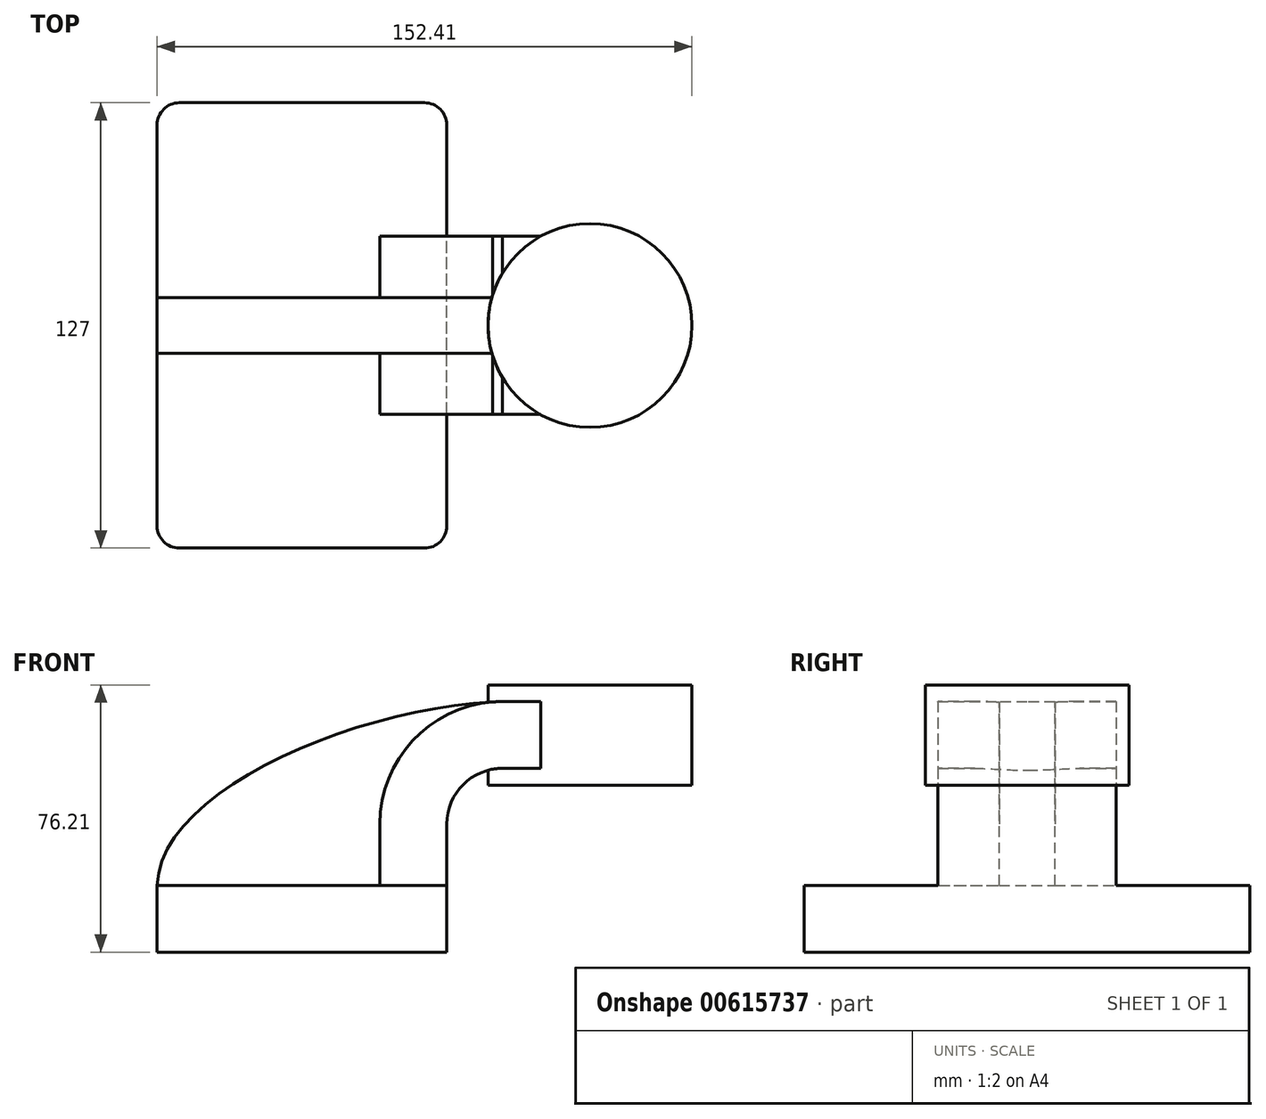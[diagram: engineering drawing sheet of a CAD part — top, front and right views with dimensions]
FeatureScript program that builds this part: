
annotation { "Feature Type Name" : "Feature", "Feature Type Description" : "" }
export const myFeature = defineFeature(function(context is Context, id is Id, definition is map)
    precondition{}
    {
        {
            var Q0;
            Q0=qCreatedBy(makeId("Front.planeOp"),FACE);
            var sketch = newSketch(context, id + "F0", { "sketchPlane" : qUnion([Q0])});
            skLineSegment(sketch, "E0.bottom", {"start": v(-41.27, -9.53) * mm, "end": v(41.28, -9.53) * mm});
            skLineSegment(sketch, "E0.top", {"start": v(-41.28, 9.52) * mm, "end": v(41.28, 9.52) * mm});
            skLineSegment(sketch, "E0.left", {"start": v(-41.28, -9.53) * mm, "end": v(-41.28, 9.53) * mm});
            skLineSegment(sketch, "E0.right", {"start": v(41.28, -9.53) * mm, "end": v(41.28, 9.52) * mm});
            skPoint(sketch, "E0.middle", {"position": v(0, 0) * mm});
            skLineSegment(sketch, "E1.bottom", {"start": v(60.32, 38.1) * mm, "end": v(111.12, 38.1) * mm});
            skLineSegment(sketch, "E1.top", {"start": v(60.32, 66.67) * mm, "end": v(111.12, 66.67) * mm});
            skLineSegment(sketch, "E1.left", {"start": v(60.32, 38.1) * mm, "end": v(60.32, 66.67) * mm});
            skLineSegment(sketch, "E1.right", {"start": v(111.12, 38.1) * mm, "end": v(111.12, 66.67) * mm});
            skPoint(sketch, "E1.middle", {"position": v(85.72, 52.39) * mm});
            skLineSegment(sketch, "E2", {"start": v(41.28, 9.52) * mm, "end": v(41.28, 27) * mm});
            skArc(sketch, "E3", {"start": v(57.15, 42.88) * mm, "mid": v(45.92, 38.23) * mm, "end": v(41.27, 27) * mm});
            skLineSegment(sketch, "E4", {"start": v(57.15, 42.88) * mm, "end": v(82.07, 42.88) * mm});
            skLineSegment(sketch, "E5.0", {"start": v(57.15, 61.93) * mm, "end": v(82.07, 61.93) * mm});
            skArc(sketch, "E5.1", {"start": v(57.15, 61.93) * mm, "mid": v(32.45, 51.7) * mm, "end": v(22.22, 27) * mm});
            skLineSegment(sketch, "E5.2", {"start": v(22.22, 9.52) * mm, "end": v(22.22, 27) * mm});
            skFitSpline(sketch, "E6", {"points": [v(-41.27, 9.53) * mm, v(57.15, 61.93) * mm], "startDerivative": vector(2.8, 83.11) * mm, "endDerivative": vector(120.3, 3.3) * mm});
            skLineSegment(sketch, "E7", {"start": v(82.07, 38.1) * mm, "end": v(82.07, 66.67) * mm});
            skSolve(sketch);
        }
        {
            var Q0;
            Q0=makeQuery(id+"F0.imprint","IMPRINT",FACE,{"disambiguationData":[TD([[makeQuery(id+"F0.imprint","IMPRINT",EDGE,{"derivedFrom":sQuery(id+"F0.wireOp",EDGE,"E0.bottom")}),1.0]])]});
            extrude(context, id + "F1", {"entities" : qUnion([Q0]), "endBound" : BoundingType.SYMMETRIC, "depth" : 127 * mm, "offsetDistance" : 25.4 * mm});
        }
        {
            var Q0;
            {var subQ1=sQuery(id+"F0.wireOp",EDGE,"E2");Q0=makeQuery(id+"F0.imprint","IMPRINT",FACE,{"disambiguationData":[TD([[makeQuery(id+"F0.imprint","IMPRINT",EDGE,{"derivedFrom":subQ1}),1.0]])]});}
            var Q1;
            {var subQ0=sQuery(id+"F0.wireOp",EDGE,"E4");var subQ1=sQuery(id+"F0.wireOp",EDGE,"E1.left");var subQ2=makeQuery(id+"F0.imprint","INTERSECT",VERTEX,{"derivedFrom":[subQ1,subQ0]});Q1=makeQuery(id+"F0.imprint","IMPRINT",FACE,{"disambiguationData":[TD([[makeQuery(id+"F0.imprint","IMPRINT",EDGE,{"disambiguationData":[TD([[subQ2,-1.0]])],"derivedFrom":subQ1}),-1.0]])]});}
            extrude(context, id + "F2", {"entities" : qUnion([Q0, Q1]), "operationType" : NewBodyOperationType.ADD, "endBound" : BoundingType.SYMMETRIC, "depth" : 50.8 * mm, "offsetDistance" : 25.4 * mm});
        }
        {
            var Q0;
            {var subQ3=sQuery(id+"F0.wireOp",EDGE,"E5.2");Q0=makeQuery(id+"F0.imprint","IMPRINT",FACE,{"disambiguationData":[TD([[makeQuery(id+"F0.imprint","IMPRINT",EDGE,{"derivedFrom":subQ3}),1.0]])]});}
            extrude(context, id + "F3", {"entities" : qUnion([Q0]), "operationType" : NewBodyOperationType.ADD, "endBound" : BoundingType.SYMMETRIC, "depth" : 15.88 * mm, "offsetDistance" : 25.4 * mm});
        }
        {
            var Q0;
            {var subQ4=sQuery(id+"F0.wireOp",EDGE,"E1.right");Q0=makeQuery(id+"F0.imprint","IMPRINT",FACE,{"disambiguationData":[TD([[makeQuery(id+"F0.imprint","IMPRINT",EDGE,{"derivedFrom":subQ4}),1.0]])]});}
            var Q1;
            Q1=sQuery(id+"F0.wireOp",EDGE,"E7");
            revolve(context, id + "F4", {"operationType" : NewBodyOperationType.ADD, "entities" : qUnion([Q0]), "axis" : qUnion([Q1]), "revolveType" : RevolveType.FULL});
        }
        {
            var Q0;
            Q0=makeQuery(id+"F1.opExtrude","CAP_EDGE",EDGE,{"disambiguationData":[OSD([sQuery(id+"F0.wireOp",EDGE,"E0.right")])],"isStart":false});
            var Q1;
            Q1=makeQuery(id+"F1.opExtrude","CAP_EDGE",EDGE,{"disambiguationData":[OSD([sQuery(id+"F0.wireOp",EDGE,"E0.left")])],"isStart":false});
            var Q2;
            Q2=makeQuery(id+"F1.opExtrude","CAP_EDGE",EDGE,{"disambiguationData":[OSD([sQuery(id+"F0.wireOp",EDGE,"E0.left")])],"isStart":true});
            var Q3;
            Q3=makeQuery(id+"F1.opExtrude","CAP_EDGE",EDGE,{"disambiguationData":[OSD([sQuery(id+"F0.wireOp",EDGE,"E0.right")])],"isStart":true});
            fillet(context, id + "F5", {"entities" : qUnion([Q0, Q1, Q2, Q3]), "radius" : 6.35 * mm, "tangentPropagation" : true, "allowEdgeOverflow" : false});
        }
    });
